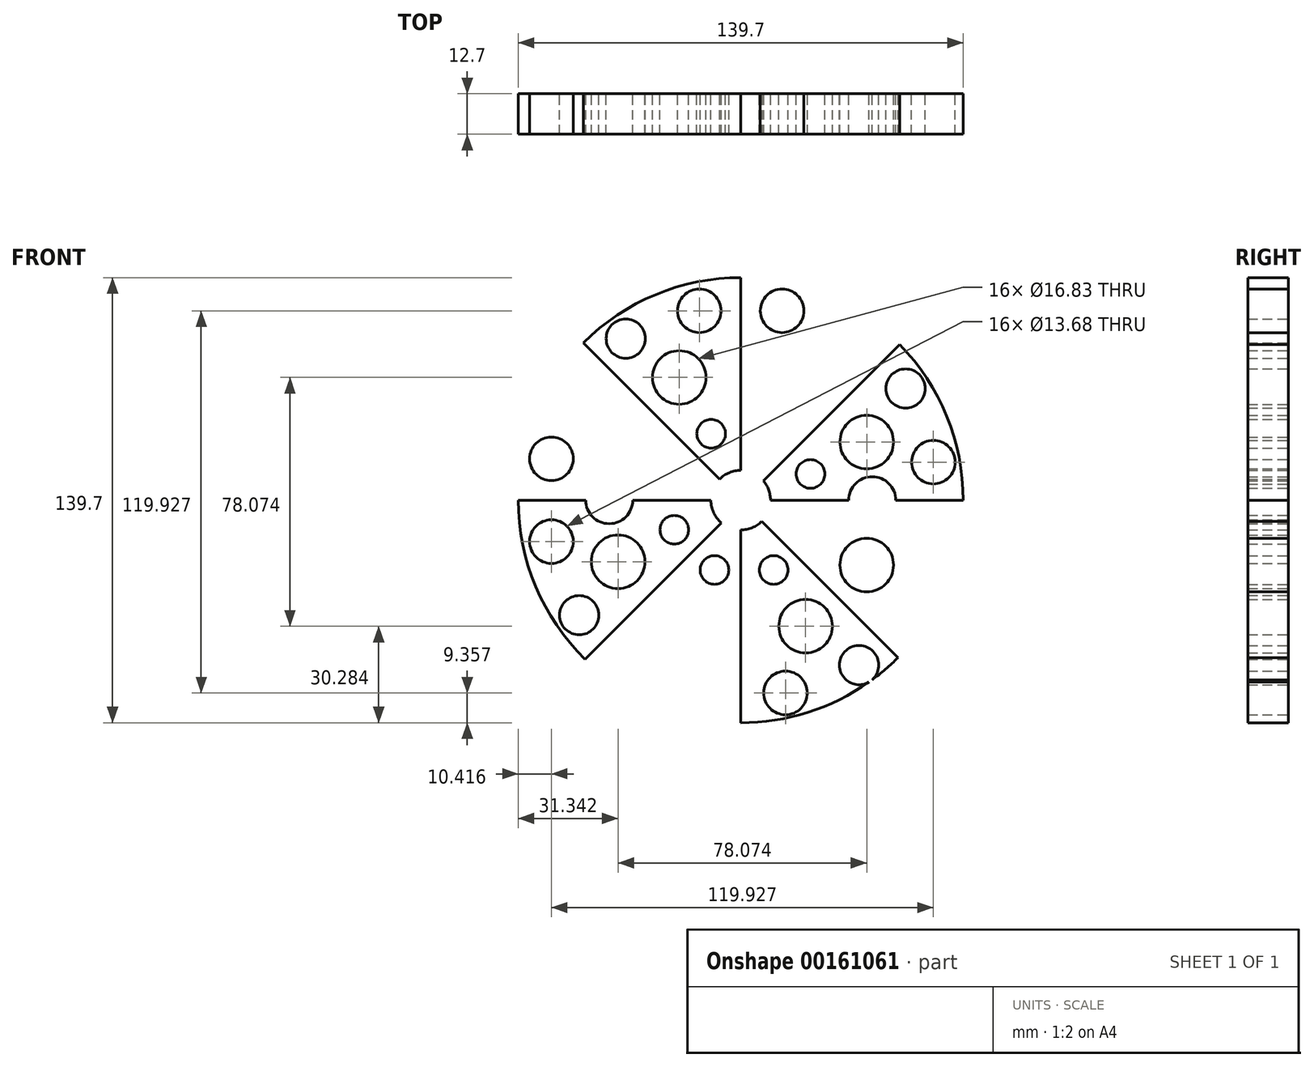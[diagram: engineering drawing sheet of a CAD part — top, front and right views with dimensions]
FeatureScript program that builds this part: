
annotation { "Feature Type Name" : "Feature", "Feature Type Description" : "" }
export const myFeature = defineFeature(function(context is Context, id is Id, definition is map)
    precondition{}
    {
        {
            var Q0;
            Q0=qCreatedBy(makeId("Front.planeOp"),FACE);
            var sketch = newSketch(context, id + "F0", { "sketchPlane" : qUnion([Q0])});
            skCircle(sketch, "E0", {"center": v(0, 0) * mm, "radius": 76.2 * mm});
            skLineSegment(sketch, "E1", {"start": v(0, 0) * mm, "end": v(76.2, 0) * mm});
            skLineSegment(sketch, "E2", {"start": v(76.2, 0) * mm, "end": v(0, 0) * mm});
            skLineSegment(sketch, "E3", {"start": v(0, -76.2) * mm, "end": v(0, 0) * mm});
            skLineSegment(sketch, "E4", {"start": v(0, 0) * mm, "end": v(0, 76.2) * mm});
            skLineSegment(sketch, "E5", {"start": v(0, 76.2) * mm, "end": v(0, 0) * mm});
            skLineSegment(sketch, "E6", {"start": v(-76.2, 0) * mm, "end": v(0, 0) * mm});
            skLineSegment(sketch, "E7", {"start": v(54.4, 53.35) * mm, "end": v(-54.51, -55.57) * mm});
            skLineSegment(sketch, "E8", {"start": v(-53.88, 53.88) * mm, "end": v(0, 0) * mm});
            skLineSegment(sketch, "E9", {"start": v(53.88, -53.88) * mm, "end": v(0, 0) * mm});
            skCircle(sketch, "E10.0", {"center": v(0, 0) * mm, "radius": 69.85 * mm});
            skCircle(sketch, "E11", {"center": v(-13, 59.43) * mm, "radius": 6.84 * mm});
            skCircle(sketch, "E12", {"center": v(-19.31, 38.5) * mm, "radius": 8.41 * mm});
            skCircle(sketch, "E13", {"center": v(-36.1, 50.71) * mm, "radius": 6.15 * mm});
            skCircle(sketch, "E14", {"center": v(-9.29, 20.85) * mm, "radius": 4.5 * mm});
            skCircle(sketch, "E15.MirrorC", {"center": v(39.57, -20.37) * mm, "radius": 8.41 * mm});
            skCircle(sketch, "E16.MirrorC", {"center": v(51.77, -37.16) * mm, "radius": 6.15 * mm});
            skCircle(sketch, "E17.MirrorC", {"center": v(60.5, -14.05) * mm, "radius": 6.84 * mm});
            skCircle(sketch, "E18.MirrorC", {"center": v(21.9, -10.35) * mm, "radius": 4.5 * mm});
            skCircle(sketch, "E19.MirrorC", {"center": v(13, 59.43) * mm, "radius": 6.84 * mm});
            skCircle(sketch, "E20.MirrorC", {"center": v(19.31, 38.5) * mm, "radius": 8.41 * mm});
            skCircle(sketch, "E21.MirrorC", {"center": v(36.1, 50.71) * mm, "radius": 6.15 * mm});
            skCircle(sketch, "E22.MirrorC", {"center": v(9.29, 20.85) * mm, "radius": 4.5 * mm});
            skCircle(sketch, "E23.MirrorC", {"center": v(-38.5, -19.31) * mm, "radius": 8.41 * mm});
            skCircle(sketch, "E24.MirrorC", {"center": v(-59.43, -13) * mm, "radius": 6.84 * mm});
            skCircle(sketch, "E25.MirrorC", {"center": v(-50.71, -36.1) * mm, "radius": 6.15 * mm});
            skCircle(sketch, "E26.MirrorC", {"center": v(-20.85, -9.29) * mm, "radius": 4.5 * mm});
            skCircle(sketch, "E27.MirrorC", {"center": v(-59.43, 13) * mm, "radius": 6.84 * mm});
            skCircle(sketch, "E28.MirrorC", {"center": v(-38.5, 19.31) * mm, "radius": 8.41 * mm});
            skCircle(sketch, "E29.MirrorC", {"center": v(-50.71, 36.1) * mm, "radius": 6.15 * mm});
            skCircle(sketch, "E30.MirrorC", {"center": v(-20.85, 9.29) * mm, "radius": 4.5 * mm});
            skCircle(sketch, "E31.MirrorC", {"center": v(-8.23, -21.9) * mm, "radius": 4.5 * mm});
            skCircle(sketch, "E32.MirrorC", {"center": v(-18.26, -39.57) * mm, "radius": 8.41 * mm});
            skCircle(sketch, "E33.MirrorC", {"center": v(-35.04, -51.77) * mm, "radius": 6.15 * mm});
            skCircle(sketch, "E34.MirrorC", {"center": v(-11.93, -60.5) * mm, "radius": 6.84 * mm});
            skCircle(sketch, "E35.MirrorC", {"center": v(39.57, 18.26) * mm, "radius": 8.41 * mm});
            skCircle(sketch, "E36.MirrorC", {"center": v(21.9, 8.23) * mm, "radius": 4.5 * mm});
            skCircle(sketch, "E37.MirrorC", {"center": v(60.5, 11.93) * mm, "radius": 6.84 * mm});
            skCircle(sketch, "E38.MirrorC", {"center": v(51.77, 35.04) * mm, "radius": 6.15 * mm});
            skCircle(sketch, "E39.MirrorC", {"center": v(10.35, -21.9) * mm, "radius": 4.5 * mm});
            skCircle(sketch, "E40.MirrorC", {"center": v(20.37, -39.57) * mm, "radius": 8.41 * mm});
            skCircle(sketch, "E41.MirrorC", {"center": v(14.05, -60.5) * mm, "radius": 6.84 * mm});
            skCircle(sketch, "E42.MirrorC", {"center": v(37.16, -51.77) * mm, "radius": 6.15 * mm});
            skCircle(sketch, "E43", {"center": v(0, 0) * mm, "radius": 9.35 * mm});
            skCircle(sketch, "E44", {"center": v(41.28, 0) * mm, "radius": 7.38 * mm});
            skCircle(sketch, "E45.MirrorC", {"center": v(-41.28, 0) * mm, "radius": 7.38 * mm});
            skSolve(sketch);
        }
        {
            var Q0;
            Q0=makeQuery(id+"F0.imprint","IMPRINT",FACE,{"disambiguationData":[TD([[makeQuery(id+"F0.imprint","IMPRINT",EDGE,{"derivedFrom":sQuery(id+"F0.wireOp",EDGE,"E11")}),-1.0]])]});
            var Q1;
            Q1=makeQuery(id+"F0.imprint","IMPRINT",FACE,{"disambiguationData":[TD([[makeQuery(id+"F0.imprint","IMPRINT",EDGE,{"derivedFrom":sQuery(id+"F0.wireOp",EDGE,"E19.MirrorC")}),1.0]])]});
            var Q2;
            Q2=makeQuery(id+"F0.imprint","IMPRINT",FACE,{"disambiguationData":[TD([[makeQuery(id+"F0.imprint","IMPRINT",EDGE,{"derivedFrom":sQuery(id+"F0.wireOp",EDGE,"E35.MirrorC")}),-1.0]])]});
            var Q3;
            Q3=makeQuery(id+"F0.imprint","IMPRINT",FACE,{"disambiguationData":[TD([[makeQuery(id+"F0.imprint","IMPRINT",EDGE,{"derivedFrom":sQuery(id+"F0.wireOp",EDGE,"E15.MirrorC")}),1.0]])]});
            var Q4;
            Q4=makeQuery(id+"F0.imprint","IMPRINT",FACE,{"disambiguationData":[TD([[makeQuery(id+"F0.imprint","IMPRINT",EDGE,{"derivedFrom":sQuery(id+"F0.wireOp",EDGE,"E39.MirrorC")}),-1.0]])]});
            var Q5;
            Q5=makeQuery(id+"F0.imprint","IMPRINT",FACE,{"disambiguationData":[TD([[makeQuery(id+"F0.imprint","IMPRINT",EDGE,{"derivedFrom":sQuery(id+"F0.wireOp",EDGE,"E31.MirrorC")}),1.0]])]});
            var Q6;
            Q6=makeQuery(id+"F0.imprint","IMPRINT",FACE,{"disambiguationData":[TD([[makeQuery(id+"F0.imprint","IMPRINT",EDGE,{"derivedFrom":sQuery(id+"F0.wireOp",EDGE,"E24.MirrorC")}),-1.0]])]});
            var Q7;
            Q7=makeQuery(id+"F0.imprint","IMPRINT",FACE,{"disambiguationData":[TD([[makeQuery(id+"F0.imprint","IMPRINT",EDGE,{"derivedFrom":sQuery(id+"F0.wireOp",EDGE,"E27.MirrorC")}),1.0]])]});
            extrude(context, id + "F1", {"entities" : qUnion([Q0, Q1, Q2, Q3, Q4, Q5, Q6, Q7]), "endBound" : BoundingType.SYMMETRIC, "depth" : 12.7 * mm});
        }
    });
